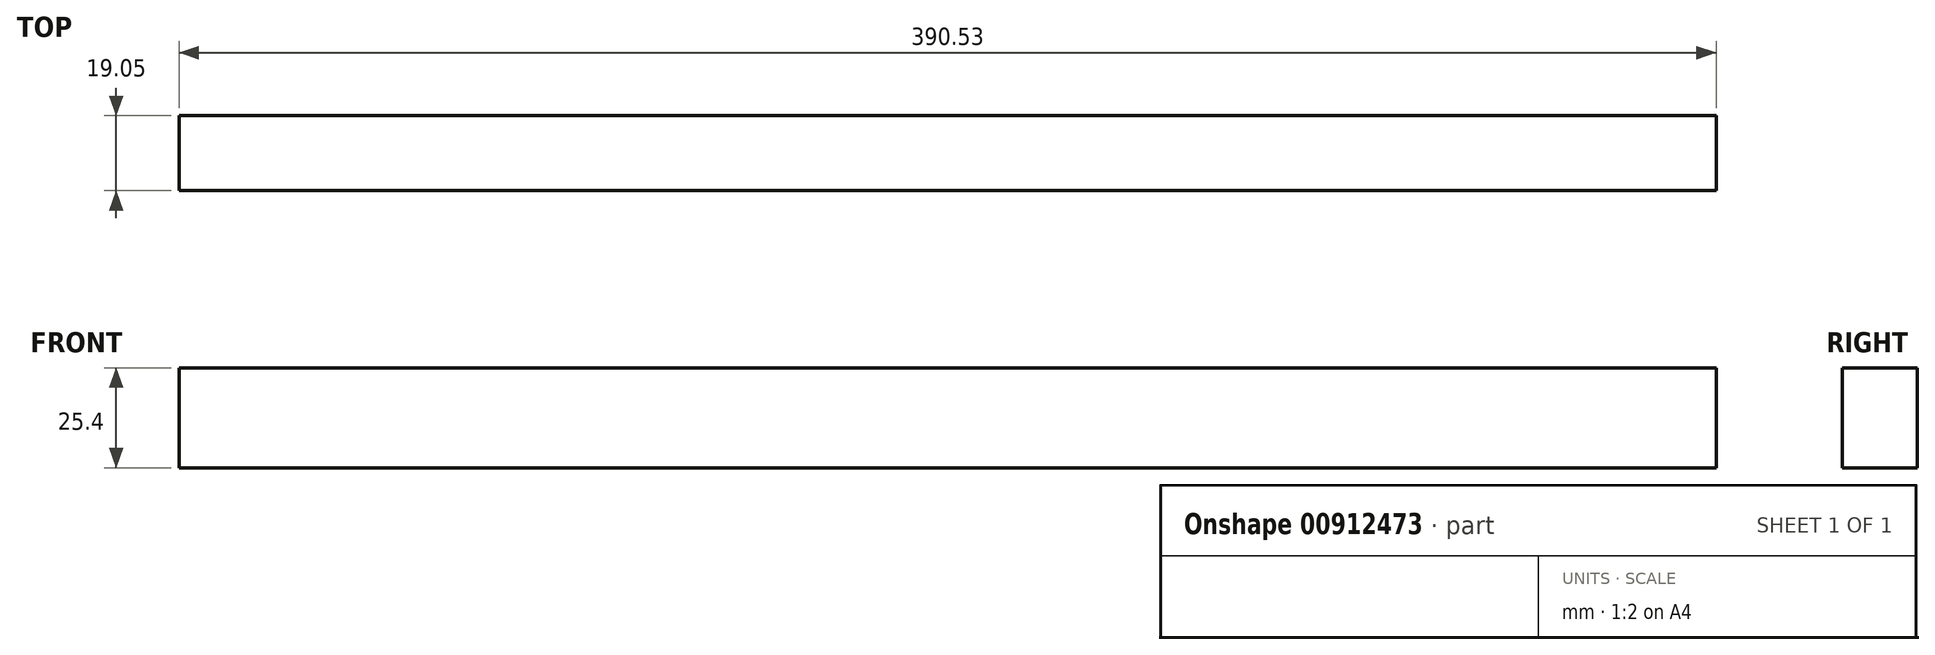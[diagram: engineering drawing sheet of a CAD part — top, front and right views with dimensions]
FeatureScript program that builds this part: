
annotation { "Feature Type Name" : "Feature", "Feature Type Description" : "" }
export const myFeature = defineFeature(function(context is Context, id is Id, definition is map)
    precondition{}
    {
        {
            var Q0;
            Q0=qCreatedBy(makeId("Right.planeOp"),FACE);
            var sketch = newSketch(context, id + "F0", { "sketchPlane" : qUnion([Q0])});
            skLineSegment(sketch, "E0.bottom", {"start": v(0, 0) * mm, "end": v(19.05, 0) * mm});
            skLineSegment(sketch, "E0.top", {"start": v(0, 25.4) * mm, "end": v(19.05, 25.4) * mm});
            skLineSegment(sketch, "E0.left", {"start": v(0, 0) * mm, "end": v(0, 25.4) * mm});
            skLineSegment(sketch, "E0.right", {"start": v(19.05, 0) * mm, "end": v(19.05, 25.4) * mm});
            skSolve(sketch);
        }
        {
            var Q0;
            Q0 = qSketchRegion(id + "F0", true);
            extrude(context, id + "F1", {"entities" : qUnion([Q0]), "depth" : 390.52 * mm, "offsetDistance" : 25.4 * mm});
        }
    });
